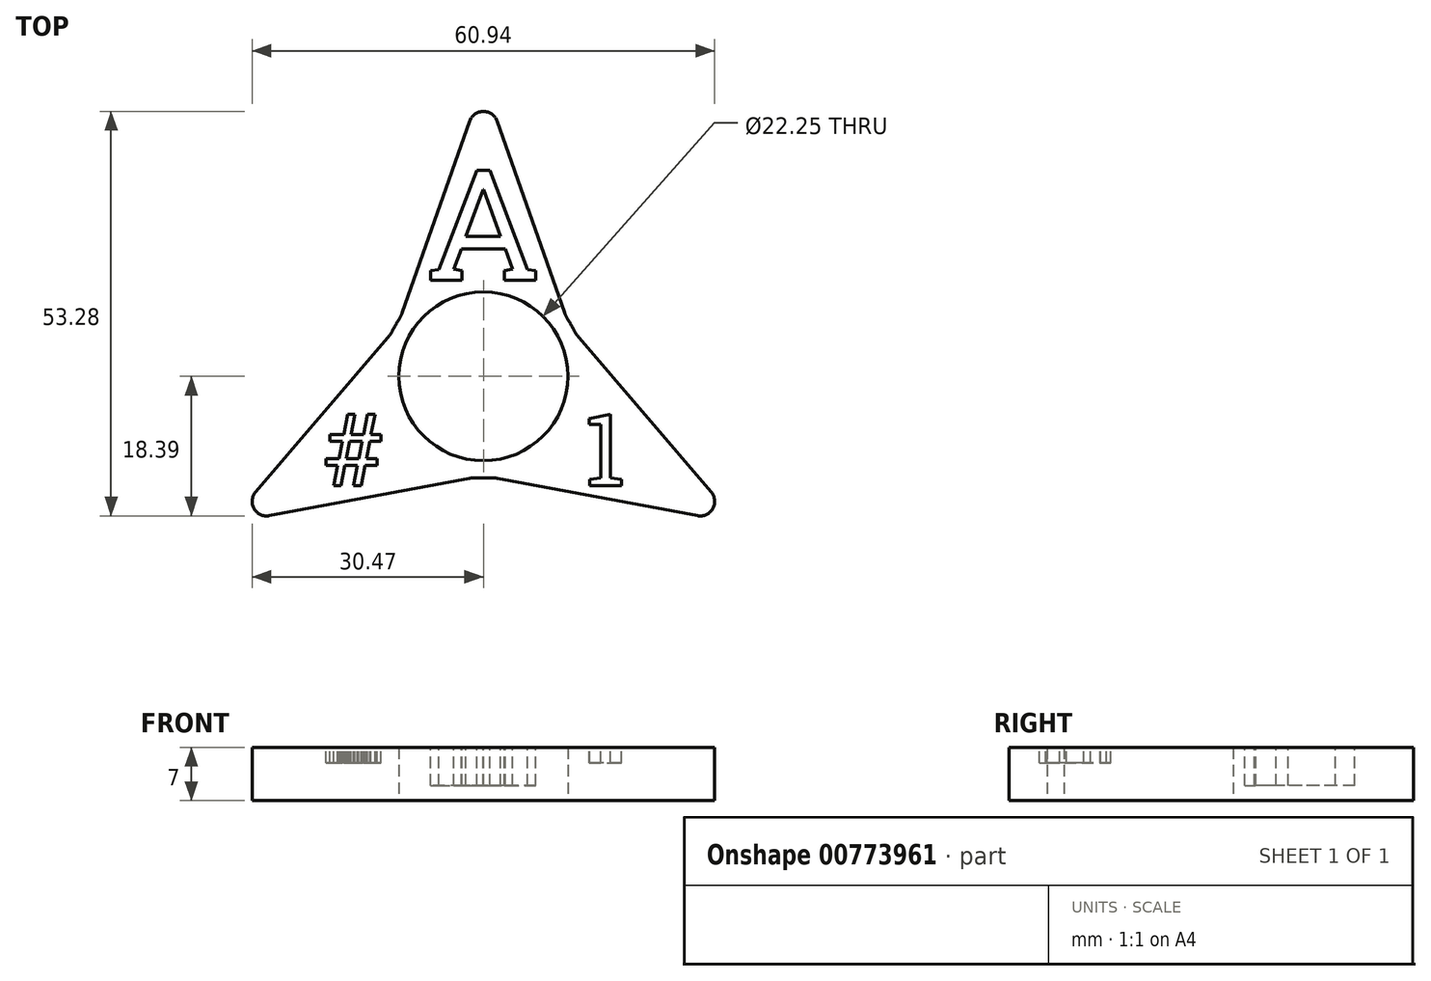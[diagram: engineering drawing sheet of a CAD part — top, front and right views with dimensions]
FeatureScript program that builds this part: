
annotation { "Feature Type Name" : "Feature", "Feature Type Description" : "" }
export const myFeature = defineFeature(function(context is Context, id is Id, definition is map)
    precondition{}
    {
        {
            var Q0;
            Q0=qCreatedBy(makeId("Top.planeOp"),FACE);
            var sketch = newSketch(context, id + "F0", { "sketchPlane" : qUnion([Q0])});
            skCircle(sketch, "E0", {"center": v(0, 0) * mm, "radius": 11.13 * mm});
            skCircle(sketch, "E1", {"center": v(0, 0) * mm, "radius": 13.4 * mm});
            skLineSegment(sketch, "E2", {"start": v(-10.92, 7.76) * mm, "end": v(0, 38.7) * mm});
            skLineSegment(sketch, "E3.MirrorCS", {"start": v(10.92, 7.76) * mm, "end": v(0, 38.7) * mm});
            skLineSegment(sketch, "E4.1.0", {"start": v(-1.26, -13.33) * mm, "end": v(-33.51, -19.35) * mm});
            skLineSegment(sketch, "E4.1.1", {"start": v(-12.18, 5.57) * mm, "end": v(-33.51, -19.35) * mm});
            skLineSegment(sketch, "E4.2.0", {"start": v(12.18, 5.57) * mm, "end": v(33.51, -19.35) * mm});
            skLineSegment(sketch, "E4.2.1", {"start": v(1.26, -13.33) * mm, "end": v(33.51, -19.35) * mm});
            skSolve(sketch);
        }
        {
            var Q0;
            Q0=qSketchRegion(id+"F0",true);
            extrude(context, id + "F1", {"entities" : qUnion([Q0]), "depth" : 7 * mm, "offsetDistance" : 25 * mm});
        }
        {
            var Q0;
            Q0=makeQuery(id+"F1.opExtrude","SWEPT_EDGE",EDGE,{"disambiguationData":[OSD([sQuery(id+"F0.wireOp",EDGE,"E4.2.0"),sQuery(id+"F0.wireOp",EDGE,"E4.2.1")])]});
            var Q1;
            Q1=makeQuery(id+"F1.opExtrude","SWEPT_EDGE",EDGE,{"disambiguationData":[OSD([sQuery(id+"F0.wireOp",EDGE,"E2"),sQuery(id+"F0.wireOp",EDGE,"E3.MirrorCS")])]});
            var Q2;
            Q2=makeQuery(id+"F1.opExtrude","SWEPT_EDGE",EDGE,{"disambiguationData":[OSD([sQuery(id+"F0.wireOp",EDGE,"E4.1.0"),sQuery(id+"F0.wireOp",EDGE,"E4.1.1")])]});
            fillet(context, id + "F2", {"entities" : qUnion([Q0, Q1, Q2]), "radius" : 1.9 * mm, "tangentPropagation" : true, "allowEdgeOverflow" : false});
        }
        {
            var Q0;
            Q0=makeQuery(id+"F1.opExtrude","SWEPT_EDGE",EDGE,{"disambiguationData":[OSD([sQuery(id+"F0.wireOp",EDGE,"E1"),sQuery(id+"F0.wireOp",EDGE,"E2")])]});
            var Q1;
            Q1=makeQuery(id+"F1.opExtrude","SWEPT_EDGE",EDGE,{"disambiguationData":[OSD([sQuery(id+"F0.wireOp",EDGE,"E1"),sQuery(id+"F0.wireOp",EDGE,"E4.1.1")])]});
            var Q2;
            Q2=makeQuery(id+"F1.opExtrude","SWEPT_EDGE",EDGE,{"disambiguationData":[OSD([sQuery(id+"F0.wireOp",EDGE,"E1"),sQuery(id+"F0.wireOp",EDGE,"E3.MirrorCS")])]});
            var Q3;
            Q3=makeQuery(id+"F1.opExtrude","SWEPT_EDGE",EDGE,{"disambiguationData":[OSD([sQuery(id+"F0.wireOp",EDGE,"E1"),sQuery(id+"F0.wireOp",EDGE,"E4.2.0")])]});
            var Q4;
            Q4=makeQuery(id+"F1.opExtrude","SWEPT_EDGE",EDGE,{"disambiguationData":[OSD([sQuery(id+"F0.wireOp",EDGE,"E1"),sQuery(id+"F0.wireOp",EDGE,"E4.2.1")])]});
            var Q5;
            Q5=makeQuery(id+"F1.opExtrude","SWEPT_EDGE",EDGE,{"disambiguationData":[OSD([sQuery(id+"F0.wireOp",EDGE,"E1"),sQuery(id+"F0.wireOp",EDGE,"E4.1.0")])]});
            fillet(context, id + "F3", {"entities" : qUnion([Q0, Q1, Q2, Q3, Q4, Q5]), "radius" : 5 * mm, "tangentPropagation" : true, "allowEdgeOverflow" : false});
        }
        {
            var Q0;
            Q0=makeQuery(id+"F1.opExtrude","CAP_FACE",FACE,{"disambiguationData":[OSD([sQuery(id+"F0.wireOp",EDGE,"E0"),sQuery(id+"F0.wireOp",EDGE,"E1"),sQuery(id+"F0.wireOp",EDGE,"E2"),sQuery(id+"F0.wireOp",EDGE,"E3.MirrorCS"),sQuery(id+"F0.wireOp",EDGE,"E4.1.0"),sQuery(id+"F0.wireOp",EDGE,"E4.1.1"),sQuery(id+"F0.wireOp",EDGE,"E4.2.0"),sQuery(id+"F0.wireOp",EDGE,"E4.2.1")])],"isStart":false});
            var sketch = newSketch(context, id + "F4", { "sketchPlane" : qUnion([Q0])});
            skText(sketch, "E5", { "text": "A\n", "fontName": "RobotoSlab-Regular.ttf"});
            const initialGuessF4  = {"E5": [-0.0075, 0.01266, 1, 0, 0.01465]};
            skSetInitialGuess(sketch, initialGuessF4);
            skSolve(sketch);
        }
        {
            var Q0;
            Q0=qSketchRegion(id+"F4",true);
            extrude(context, id + "F5", {"entities" : qUnion([Q0]), "operationType" : NewBodyOperationType.REMOVE, "oppositeDirection" : true, "depth" : 5 * mm, "offsetDistance" : 25 * mm});
        }
        {
            var Q0;
            {var subQ0=sQuery(id+"F0.wireOp",EDGE,"E4.2.0");var subQ1=sQuery(id+"F0.wireOp",EDGE,"E1");var subQ2=sQuery(id+"F0.wireOp",EDGE,"E3.MirrorCS");var subQ3=sQuery(id+"F0.wireOp",EDGE,"E4.1.1");var subQ4=sQuery(id+"F0.wireOp",EDGE,"E2");var subQ5=sQuery(id+"F0.wireOp",EDGE,"E4.1.0");var subQ6=sQuery(id+"F0.wireOp",EDGE,"E4.2.1");var subQ7=sQuery(id+"F0.wireOp",EDGE,"E0");Q0=makeQuery(id+"F5.boolean.opBoolean","SPLIT",FACE,{"disambiguationData":[TD([makeQuery(id+"F1.opExtrude","SWEPT_FACE",FACE,{"disambiguationData":[OSD([subQ7])]})])],"derivedFrom":makeQuery(id+"F1.opExtrude","CAP_FACE",FACE,{"disambiguationData":[OSD([subQ7,subQ1,subQ4,subQ2,subQ5,subQ3,subQ0,subQ6])],"isStart":false})});}
            var sketch = newSketch(context, id + "F6", { "sketchPlane" : qUnion([Q0])});
            skPoint(sketch, "E6.secondSnap0", {"position": v(-21.3, -5.09) * mm});
            skText(sketch, "E7", { "text": "#        1", "fontName": "RobotoSlab-Regular.ttf"});
            const initialGuessF6  = {"E7": [-0.02113, -0.01438, 1, 0, 0.00952]};
            skSetInitialGuess(sketch, initialGuessF6);
            skSolve(sketch);
        }
        {
            var Q0;
            Q0=qSketchRegion(id+"F6",true);
            extrude(context, id + "F7", {"entities" : qUnion([Q0]), "operationType" : NewBodyOperationType.REMOVE, "oppositeDirection" : true, "depth" : 2 * mm, "offsetDistance" : 25 * mm});
        }
    });
